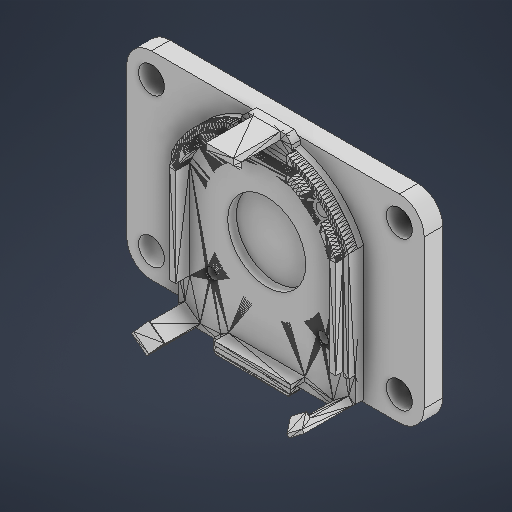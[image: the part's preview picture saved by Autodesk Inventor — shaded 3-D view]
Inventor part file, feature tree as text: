
AUTODESK INVENTOR PART (.ipt)
format: ipt  version: 2025 (Build 290162000, 162)  size: 1,857,024 bytes
history: native  units: in
note: dims shown in document units (in); Inventor stores cm internally (conversion verified against a paired STEP export)
features: extrude x7, sketch x5, plane x1, fillet x1, other x1
ambient origin geometry x8: Origin, YZ Plane, XZ Plane, XY Plane, X Axis, Y Axis, Z Axis, Center Point
bodies: Solid1 (feature_tree)
feature tree (15):
  plane  "Work Plane1"
  extrude  "Extrusion1"  Depth=0.1575in
  extrude  "Extrusion2"  Depth=0.4961in
  sketch  "Sketch3"  dims[d5=0.3937in d6=0.0in d7=0.0787in]
  extrude  "Extrusion3"  Depth=0.3937in
  extrude  "Extrusion4"  TaperAngle=0.0deg  [1 undecoded]
  sketch  "Sketch4"  dims[d8=0.1181in d9=0.0in d10=0.0in]
  extrude  "Extrusion5"  Depth=0.1575in
  extrude  "Extrusion6"  Depth=0.1575in
  extrude  "Extrusion7"  Depth=0.1575in
  fillet  "Fillet1"  Radius=0.0591in
  sketch  "Sketch1"  dims[d0=0.4803in d1=0.1575in]
  sketch  "Sketch2"  dims[d2=0.0in d3=0.0in d4=0.4961in]
  sketch  "Sketch5"  dims[d11=0.3937in d12=0.0in d13=0.0787in d14=0.0787in d15=0.0787in d16=0.0591in d17=0.0591in d18=0.0591in d19=0.0079in d20=0.0079in d21=0.0079in d22=0.0394in d23=0.0in d24=0.0394in d25=0.0in d26=1.2598in d27=1.8898in d28=1.2598in d29=0.1654in d30=0.7874in d31=0.4724in d32=0.1181in d33=0.0in d34=0.1575in]
  other  "MeshFeature1"
note: 1 required parameter value undecoded (feature->parameter linkage not recoverable at this tier; creation-order binding heuristic only, values carry confidence <= 0.55)
